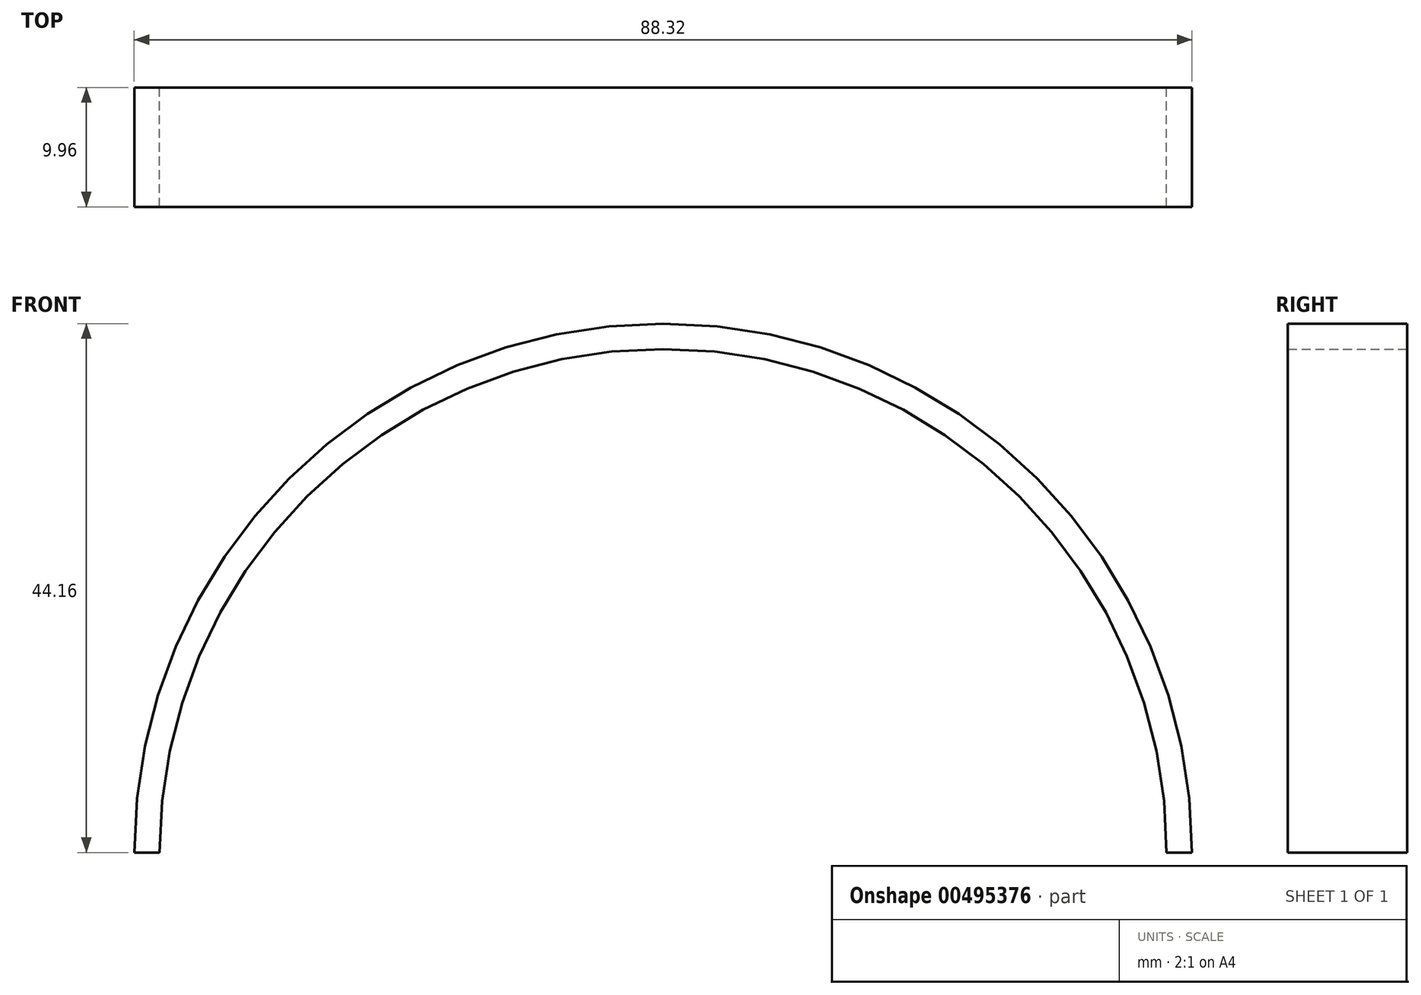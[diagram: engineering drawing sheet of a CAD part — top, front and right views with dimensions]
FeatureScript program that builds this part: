
annotation { "Feature Type Name" : "Feature", "Feature Type Description" : "" }
export const myFeature = defineFeature(function(context is Context, id is Id, definition is map)
    precondition{}
    {
        {
            var Q0;
            Q0=qCreatedBy(makeId("Front.planeOp"),FACE);
            var sketch = newSketch(context, id + "F0", { "sketchPlane" : qUnion([Q0])});
            skArc(sketch, "E0", {"start": v(43.18, 0) * mm, "mid": v(0, 43.18) * mm, "end": v(-43.18, 0) * mm});
            skPoint(sketch, "E1.orphan", {"position": v(-69.39, 0) * mm});
            skSolve(sketch);
        }
        {
            var Q0;
            Q0=qCreatedBy(makeId("Top.planeOp"),FACE);
            var sketch = newSketch(context, id + "F1", { "sketchPlane" : qUnion([Q0])});
            skPoint(sketch, "E2.middle", {"position": v(-43.1, 0) * mm});
            skPoint(sketch, "E2.bottom.start.orphan", {"position": v(-50.9, -1.32) * mm});
            skPoint(sketch, "E2.right.start.orphan", {"position": v(-35.3, -1.32) * mm});
            skPoint(sketch, "E2.top.end.orphan", {"position": v(-35.3, 1.32) * mm});
            skPoint(sketch, "E2.top.start.orphan", {"position": v(-50.9, 1.32) * mm});
            skLineSegment(sketch, "E3.bottom", {"start": v(-44.16, -4.98) * mm, "end": v(-42.04, -4.98) * mm});
            skLineSegment(sketch, "E3.top", {"start": v(-44.16, 4.98) * mm, "end": v(-42.04, 4.98) * mm});
            skLineSegment(sketch, "E3.left", {"start": v(-44.16, -4.98) * mm, "end": v(-44.16, 4.98) * mm});
            skLineSegment(sketch, "E3.right", {"start": v(-42.04, -4.98) * mm, "end": v(-42.04, 4.98) * mm});
            skSolve(sketch);
        }
        {
            var Q0;
            Q0=makeQuery(id+"F1.imprint","IMPRINT",FACE,{"disambiguationData":[TD([[makeQuery(id+"F1.imprint","IMPRINT",EDGE,{"derivedFrom":sQuery(id+"F1.wireOp",EDGE,"E3.bottom")}),1.0]])]});
            var Q1;
            Q1=sQuery(id+"F0.wireOp",EDGE,"E0");
            sweep(context, id + "F2", {"profiles" : qUnion([Q0]), "path" : qUnion([Q1])});
        }
    });
